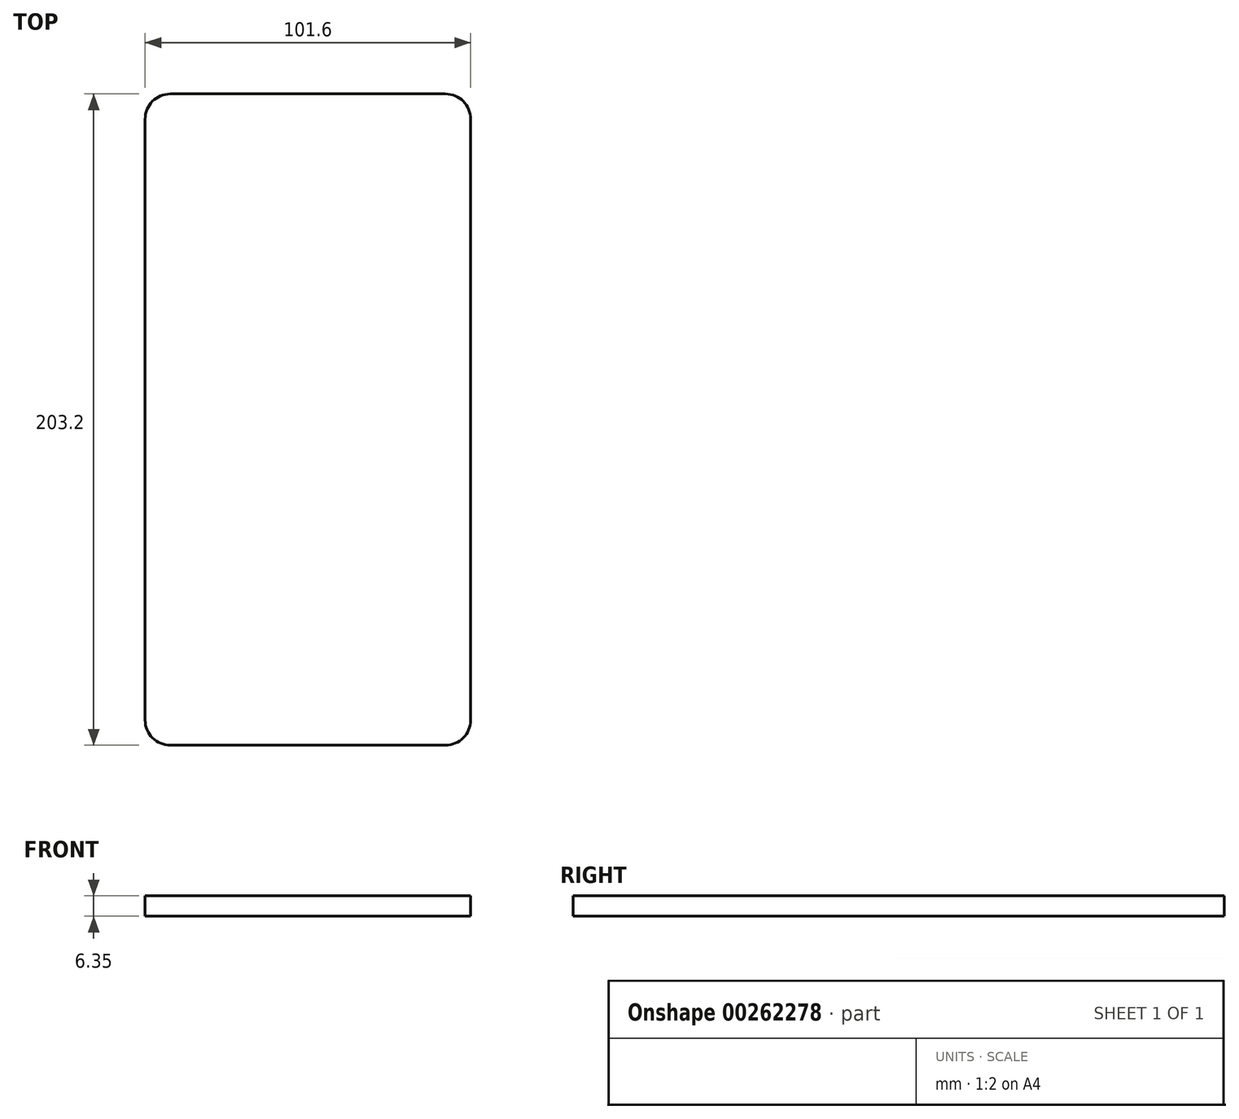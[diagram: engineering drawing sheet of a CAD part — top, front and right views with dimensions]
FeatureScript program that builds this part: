
annotation { "Feature Type Name" : "Feature", "Feature Type Description" : "" }
export const myFeature = defineFeature(function(context is Context, id is Id, definition is map)
    precondition{}
    {
        {
            var Q0;
            Q0=qCreatedBy(makeId("Top.planeOp"),FACE);
            var sketch = newSketch(context, id + "F0", { "sketchPlane" : qUnion([Q0])});
            skLineSegment(sketch, "E0.bottom", {"start": v(42.93, 101.6) * mm, "end": v(-42.93, 101.6) * mm});
            skLineSegment(sketch, "E0.top", {"start": v(42.93, -101.6) * mm, "end": v(-42.93, -101.6) * mm});
            skLineSegment(sketch, "E0.left", {"start": v(50.8, 93.73) * mm, "end": v(50.8, -93.73) * mm});
            skLineSegment(sketch, "E0.right", {"start": v(-50.8, 93.73) * mm, "end": v(-50.8, -93.73) * mm});
            skPoint(sketch, "E0.middle", {"position": v(0, 0) * mm});
            skPoint(sketch, "E1.visualSharp", {"position": v(-50.8, 101.6) * mm});
            skArc(sketch, "E1.filletArc", {"start": v(-42.93, 101.6) * mm, "mid": v(-48.5, 99.3) * mm, "end": v(-50.8, 93.73) * mm});
            skPoint(sketch, "E2.visualSharp", {"position": v(50.8, 101.6) * mm});
            skArc(sketch, "E2.filletArc", {"start": v(50.8, 93.73) * mm, "mid": v(48.5, 99.3) * mm, "end": v(42.93, 101.6) * mm});
            skPoint(sketch, "E3.visualSharp", {"position": v(50.8, -101.6) * mm});
            skArc(sketch, "E3.filletArc", {"start": v(42.93, -101.6) * mm, "mid": v(48.5, -99.3) * mm, "end": v(50.8, -93.73) * mm});
            skPoint(sketch, "E4.visualSharp", {"position": v(-50.8, -101.6) * mm});
            skArc(sketch, "E4.filletArc", {"start": v(-50.8, -93.73) * mm, "mid": v(-48.5, -99.3) * mm, "end": v(-42.93, -101.6) * mm});
            skLineSegment(sketch, "E5.bottom", {"start": v(-63.5, 114.3) * mm, "end": v(63.5, 114.3) * mm});
            skLineSegment(sketch, "E5.top", {"start": v(-63.5, -114.3) * mm, "end": v(63.5, -114.3) * mm});
            skLineSegment(sketch, "E5.left", {"start": v(-63.5, 114.3) * mm, "end": v(-63.5, -114.3) * mm});
            skLineSegment(sketch, "E5.right", {"start": v(63.5, 114.3) * mm, "end": v(63.5, -114.3) * mm});
            skSolve(sketch);
        }
        {
            var Q0;
            Q0=makeQuery(id+"F0.imprint","IMPRINT",FACE,{"disambiguationData":[TD([[makeQuery(id+"F0.imprint","IMPRINT",EDGE,{"derivedFrom":sQuery(id+"F0.wireOp",EDGE,"E0.bottom")}),1.0]])]});
            extrude(context, id + "F1", {"entities" : qUnion([Q0]), "depth" : 6.35 * mm});
        }
    });
